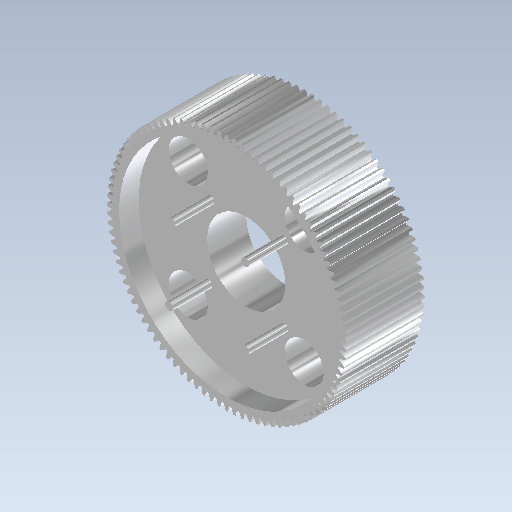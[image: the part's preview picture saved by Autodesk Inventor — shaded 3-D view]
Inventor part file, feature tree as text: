
AUTODESK INVENTOR PART (.ipt)
format: ipt  version: 2021 (Build 250183000, 183)  size: 626,688 bytes
history: native  units: mm (DEFAULTED — no unit token found)
features: sketch x7, extrude x6, plane x3, other x3
ambient origin geometry x8: Origin, YZ Plane, XZ Plane, XY Plane, X Axis, Y Axis, Z Axis, Center Point
bodies: Solid1 (feature_tree)
feature tree (19):
  extrude  "Extrusion1"  Depth=40.0mm TaperAngle=0.0deg
  plane  "Work Plane2"
  plane  "Work Plane8"
  plane  "Work Plane9"
  other  "Spur Gear"
  extrude  "Extrusion2"  Depth=10.0mm TaperAngle=0.0deg
  extrude  "Extrusion3"  Depth=0.327249mm TaperAngle=0.0deg
  extrude  "Extrusion4"  TaperAngle=0.0deg  [1 undecoded]
  extrude  "Extrusion5"  Depth=80.0mm
  extrude  "Extrusion6"  Depth=110.0mm
  sketch  "Sketch1"  dims[d0=122.5mm d1=40.0mm d2=0.0mm]
  sketch  "Sketch2"  dims[d3=120.0mm d4=10.0mm d5=0.0mm]
  other  "Srf1"
  sketch  "Sketch3"  dims[d16=80.0mm d17=0.0mm d34=0.327249mm]
  sketch  "Sketch4"  dims[d39=0.0mm d41=0.0mm]
  sketch  "Sketch5"  dims[d43=80.0mm d46=80.0mm]
  sketch  "Sketch6"  dims[d47=0.0mm d48=0.0mm d49=110.0mm]
  sketch  "Sketch7"  dims[d50=10.0mm d51=0.0mm d52=110.0mm d53=10.0mm d54=0.0mm d55=40.0mm d56=20.0mm d57=0.0mm d58=55.0mm d59=45.0deg d60=20.0mm d61=20.0mm d62=20.0mm d63=20.0mm d64=20.0mm d65=0.0mm d66=55.0mm d67=45.0deg d68=110.0mm d69=55.0mm d70=110.0mm d71=4.0mm d72=4.0mm d73=4.0mm d74=4.0mm d75=20.0mm d76=0.0mm]
  other  "Pitch Diameter"
note: 1 required parameter value undecoded (feature->parameter linkage not recoverable at this tier; creation-order binding heuristic only, values carry confidence <= 0.55)
